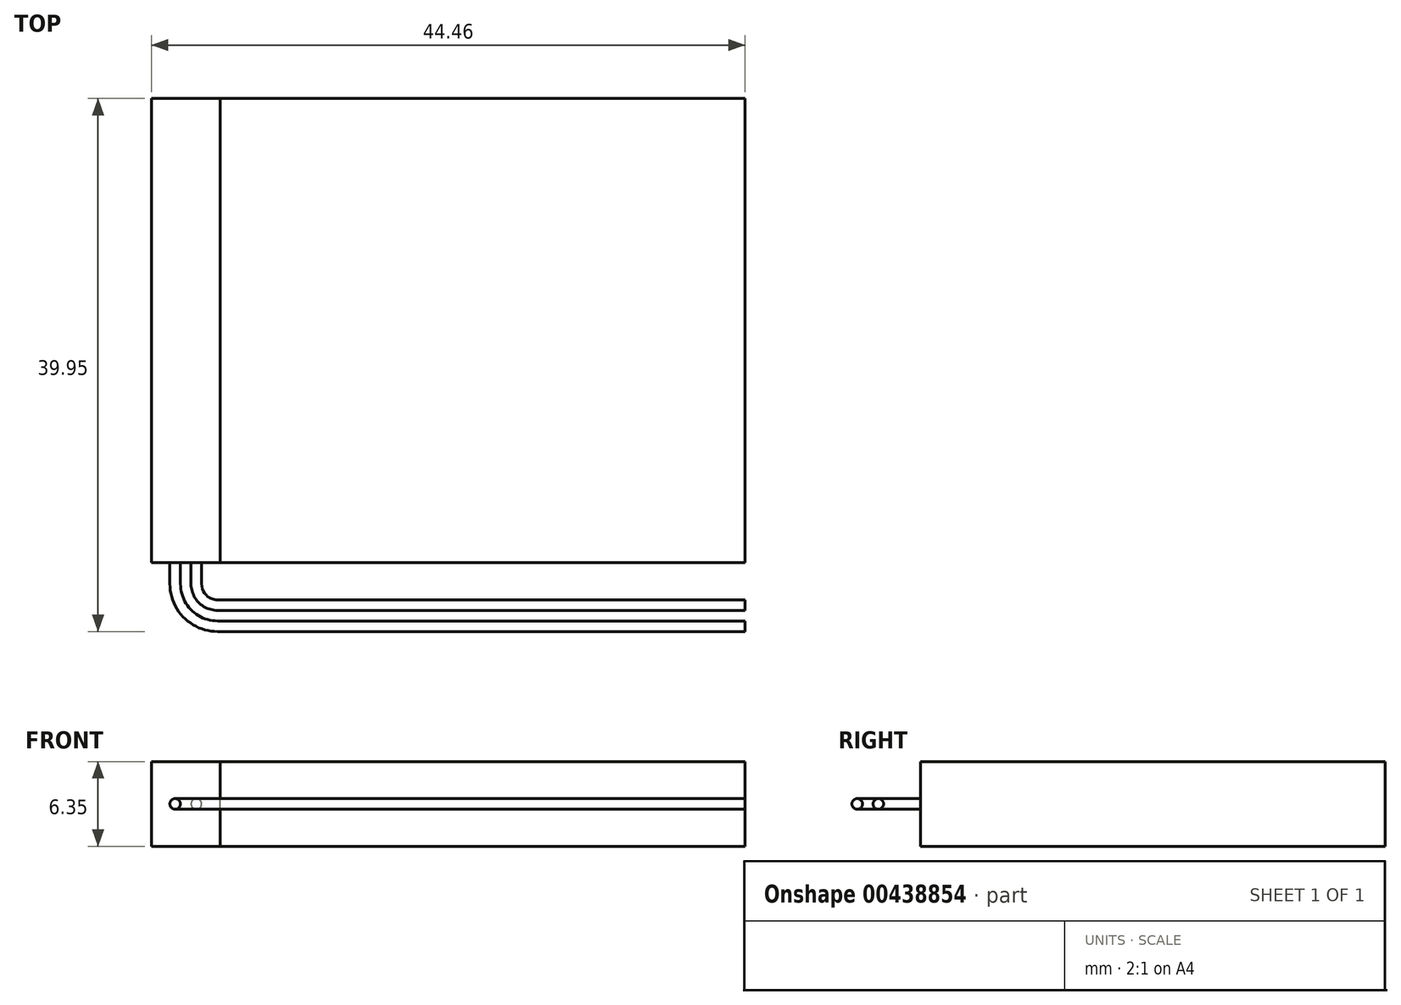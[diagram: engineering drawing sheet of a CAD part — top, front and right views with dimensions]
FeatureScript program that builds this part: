
annotation { "Feature Type Name" : "Feature", "Feature Type Description" : "" }
export const myFeature = defineFeature(function(context is Context, id is Id, definition is map)
    precondition{}
    {
        {
            var Q0;
            Q0=qCreatedBy(makeId("Top.planeOp"),FACE);
            var sketch = newSketch(context, id + "F0", { "sketchPlane" : qUnion([Q0])});
            skLineSegment(sketch, "E0.bottom", {"start": v(22.22, -17.4) * mm, "end": v(-22.23, -17.4) * mm});
            skLineSegment(sketch, "E0.top", {"start": v(22.22, 17.4) * mm, "end": v(-22.22, 17.4) * mm});
            skLineSegment(sketch, "E0.left", {"start": v(22.22, -17.4) * mm, "end": v(22.22, 17.4) * mm});
            skLineSegment(sketch, "E0.right", {"start": v(-22.22, -17.4) * mm, "end": v(-22.22, 17.4) * mm});
            skPoint(sketch, "E0.middle", {"position": v(0, 0) * mm});
            skSolve(sketch);
        }
        {
            var Q0;
            Q0 = qSketchRegion(id + "F0", true);
            extrude(context, id + "F1", {"entities" : qUnion([Q0]), "depth" : 6.35 * mm, "offsetDistance" : 25.4 * mm});
        }
        {
            var Q0;
            Q0=makeQuery(id+"F1.opExtrude","CAP_FACE",FACE,{"disambiguationData":[OSD([sQuery(id+"F0.wireOp",EDGE,"E0.bottom"),sQuery(id+"F0.wireOp",EDGE,"E0.top"),sQuery(id+"F0.wireOp",EDGE,"E0.left"),sQuery(id+"F0.wireOp",EDGE,"E0.right")])],"isStart":false});
            var sketch = newSketch(context, id + "F2", { "sketchPlane" : qUnion([Q0])});
            skLineSegment(sketch, "E1.bottom", {"start": v(-22.22, 17.4) * mm, "end": v(-17.1, 17.4) * mm});
            skLineSegment(sketch, "E1.top", {"start": v(-22.22, -17.4) * mm, "end": v(-17.1, -17.4) * mm});
            skLineSegment(sketch, "E1.left", {"start": v(-22.22, 17.4) * mm, "end": v(-22.22, -17.4) * mm});
            skLineSegment(sketch, "E1.right", {"start": v(-17.1, 17.4) * mm, "end": v(-17.1, -17.4) * mm});
            skSolve(sketch);
        }
        {
            var Q0;
            Q0=makeQuery(id+"F2.imprint","IMPRINT",FACE,{"disambiguationData":[TD([[makeQuery(id+"F2.imprint","IMPRINT",EDGE,{"derivedFrom":sQuery(id+"F2.wireOp",EDGE,"E1.bottom")}),1.0]])]});
            extrude(context, id + "F3", {"entities" : qUnion([Q0]), "operationType" : NewBodyOperationType.REMOVE, "endBound" : BoundingType.THROUGH_ALL, "oppositeDirection" : true, "depth" : 9 * mm});
        }
        {
            var Q0;
            Q0 = qSketchRegion(id + "F2", true);
            var Q1;
            Q1=makeQuery(id+"F1.opExtrude","CAP_FACE",FACE,{"disambiguationData":[OSD([sQuery(id+"F0.wireOp",EDGE,"E0.bottom"),sQuery(id+"F0.wireOp",EDGE,"E0.top"),sQuery(id+"F0.wireOp",EDGE,"E0.left"),sQuery(id+"F0.wireOp",EDGE,"E0.right")])],"isStart":true});
            extrude(context, id + "F4", {"entities" : qUnion([Q0]), "endBound" : BoundingType.UP_TO_SURFACE, "oppositeDirection" : true, "endBoundEntityFace" : qUnion([Q1]), "depth" : 9 * mm, "offsetDistance" : 25.4 * mm});
        }
        {
            var Q0;
            Q0=qCreatedBy(makeId("Top.planeOp"),FACE);
            var Q1;
            Q1=makeQuery(id+"F1.opExtrude","CAP_FACE",FACE,{"disambiguationData":[OSD([sQuery(id+"F0.wireOp",EDGE,"E0.bottom"),sQuery(id+"F0.wireOp",EDGE,"E0.top"),sQuery(id+"F0.wireOp",EDGE,"E0.left"),sQuery(id+"F0.wireOp",EDGE,"E0.right")])],"isStart":false});
            cPlane(context, id + "F5", {"entities" : qUnion([Q0, Q1]), "cplaneType" : CPlaneType.MID_PLANE, "offset" : .9 / 4 * 30 * mm, "width" : 152.4 * mm, "height" : 152.4 * mm});
        }
        {
            var Q0;
            Q0=makeQuery(id+"F4.opExtrude","SWEPT_FACE",FACE,{"disambiguationData":[OSD([sQuery(id+"F2.wireOp",EDGE,"E1.top")])]});
            var sketch = newSketch(context, id + "F6", { "sketchPlane" : qUnion([Q0])});
            skCircle(sketch, "E2", {"center": v(-20.46, 3.17) * mm, "radius": 0.4 * mm});
            skCircle(sketch, "E3", {"center": v(-18.87, 3.17) * mm, "radius": 0.4 * mm});
            skLineSegment(sketch, "E4", {"start": v(-20.46, 3.17) * mm, "end": v(-18.87, 3.17) * mm, "construction": true});
            skLineSegment(sketch, "E5", {"start": v(-19.66, 6.35) * mm, "end": v(-19.66, 0) * mm, "construction": true});
            skPoint(sketch, "E6", {"position": v(-19.66, 3.17) * mm});
            skPoint(sketch, "E7", {"position": v(-19.66, 3.18) * mm});
            skSolve(sketch);
        }
        {
            var Q0;
            Q0=qCreatedBy(id+"F5.planeOp",FACE);
            var sketch = newSketch(context, id + "F7", { "sketchPlane" : qUnion([Q0])});
            skLineSegment(sketch, "E8", {"start": v(-17.28, -20.57) * mm, "end": v(22.22, -20.57) * mm});
            skLineSegment(sketch, "E9", {"start": v(-17.28, -22.16) * mm, "end": v(22.22, -22.16) * mm});
            skLineSegment(sketch, "E10", {"start": v(-20.46, -18.99) * mm, "end": v(-20.46, -17.4) * mm});
            skLineSegment(sketch, "E11", {"start": v(-18.87, -18.99) * mm, "end": v(-18.87, -17.4) * mm});
            skArc(sketch, "E12", {"start": v(-18.87, -18.99) * mm, "mid": v(-18.4, -20.1) * mm, "end": v(-17.28, -20.57) * mm});
            skArc(sketch, "E13", {"start": v(-20.46, -18.99) * mm, "mid": v(-19.52, -21.23) * mm, "end": v(-17.28, -22.16) * mm});
            skSolve(sketch);
        }
        {
            var Q0;
            Q0=makeQuery(id+"F6.imprint","IMPRINT",FACE,{"disambiguationData":[TD([[makeQuery(id+"F6.imprint","IMPRINT",EDGE,{"derivedFrom":sQuery(id+"F6.wireOp",EDGE,"E3")}),1.0]])]});
            var Q1;
            Q1=sQuery(id+"F7.wireOp",EDGE,"E11");
            var Q2;
            Q2=sQuery(id+"F7.wireOp",EDGE,"E12");
            var Q3;
            Q3=sQuery(id+"F7.wireOp",EDGE,"E8");
            sweep(context, id + "F8", {"profiles" : qUnion([Q0]), "path" : qUnion([Q1, Q2, Q3])});
        }
        {
            var Q0;
            Q0=makeQuery(id+"F6.imprint","IMPRINT",FACE,{"disambiguationData":[TD([[makeQuery(id+"F6.imprint","IMPRINT",EDGE,{"derivedFrom":sQuery(id+"F6.wireOp",EDGE,"E2")}),1.0]])]});
            var Q1;
            Q1=sQuery(id+"F6.wireOp",EDGE,"E2");
            var Q2;
            Q2=sQuery(id+"F7.wireOp",EDGE,"E10");
            var Q3;
            Q3=sQuery(id+"F7.wireOp",EDGE,"E13");
            var Q4;
            Q4=sQuery(id+"F7.wireOp",EDGE,"E9");
            sweep(context, id + "F9", {"profiles" : qUnion([Q0]), "surfaceProfiles" : qUnion([Q1]), "path" : qUnion([Q2, Q3, Q4])});
        }
    });
